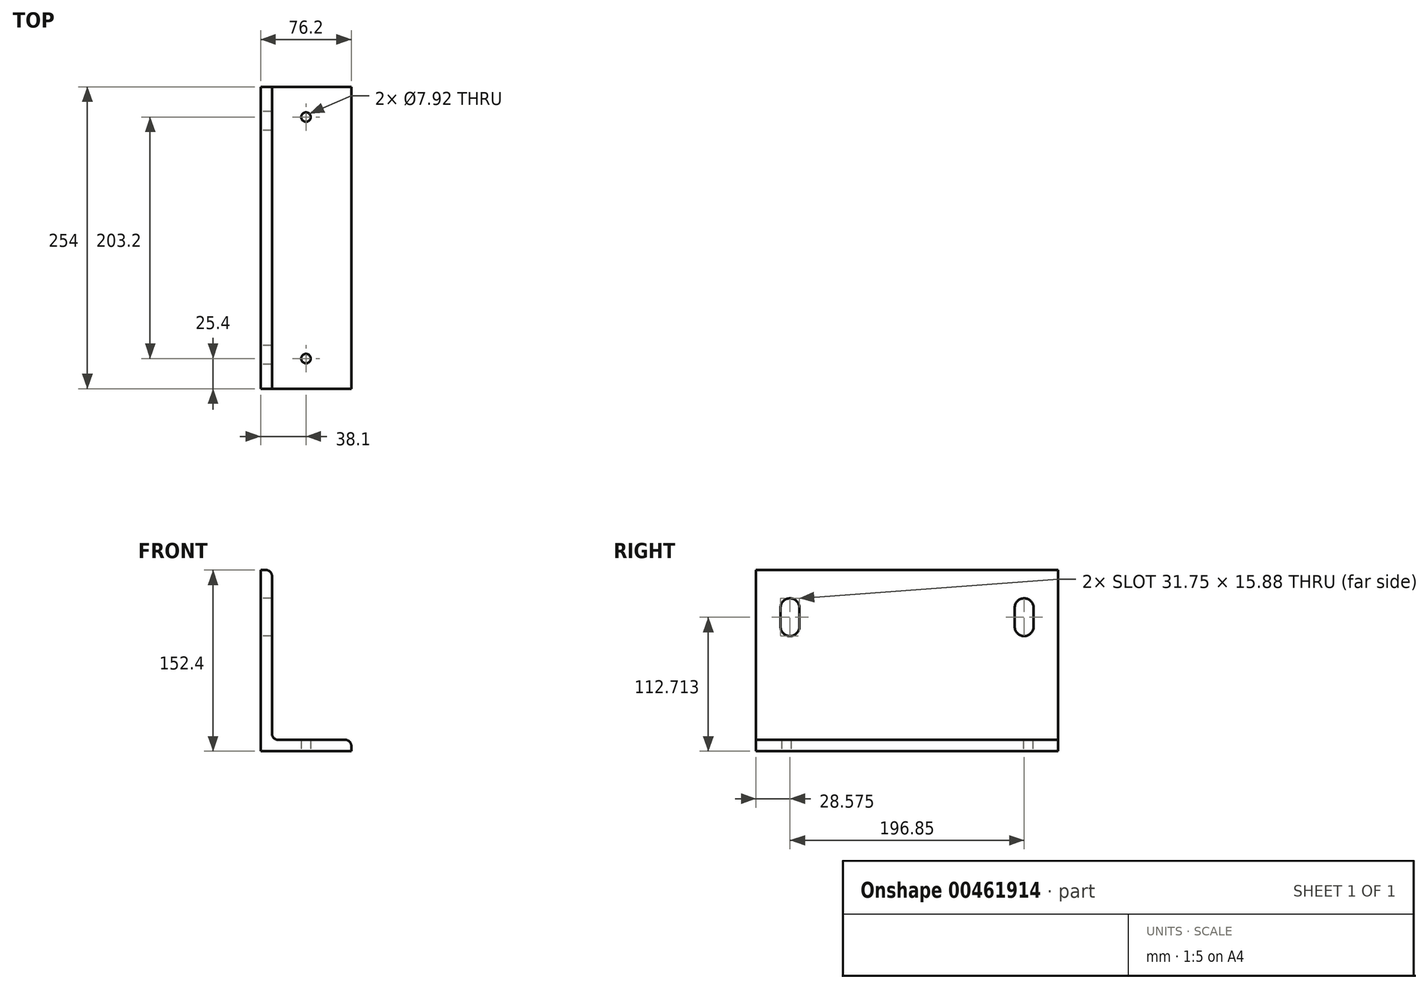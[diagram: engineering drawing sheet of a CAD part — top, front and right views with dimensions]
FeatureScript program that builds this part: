
annotation { "Feature Type Name" : "Feature", "Feature Type Description" : "" }
export const myFeature = defineFeature(function(context is Context, id is Id, definition is map)
    precondition{}
    {
        {
            var Q0;
            Q0=qCreatedBy(makeId("Front.planeOp"),FACE);
            var sketch = newSketch(context, id + "F0", { "sketchPlane" : qUnion([Q0])});
            skLineSegment(sketch, "E0", {"start": v(0, 0) * mm, "end": v(0, 152.4) * mm});
            skLineSegment(sketch, "E1", {"start": v(0, 152.4) * mm, "end": v(9.53, 152.4) * mm});
            skLineSegment(sketch, "E2", {"start": v(9.53, 152.4) * mm, "end": v(9.53, 9.53) * mm});
            skLineSegment(sketch, "E3", {"start": v(9.53, 9.53) * mm, "end": v(76.2, 9.53) * mm});
            skLineSegment(sketch, "E4", {"start": v(76.2, 9.53) * mm, "end": v(76.2, 0) * mm});
            skLineSegment(sketch, "E5", {"start": v(76.2, 0) * mm, "end": v(0, 0) * mm});
            skSolve(sketch);
        }
        {
            var Q0;
            Q0 = qSketchRegion(id + "F0", true);
            extrude(context, id + "F1", {"entities" : qUnion([Q0]), "endBound" : BoundingType.SYMMETRIC, "depth" : 254 * mm});
        }
        {
            var Q0;
            Q0=makeQuery(id+"F1.opExtrude","SWEPT_EDGE",EDGE,{"disambiguationData":[OSD([sQuery(id+"F0.wireOp",EDGE,"E1"),sQuery(id+"F0.wireOp",EDGE,"E2")])]});
            var Q1;
            Q1=makeQuery(id+"F1.opExtrude","SWEPT_EDGE",EDGE,{"disambiguationData":[OSD([sQuery(id+"F0.wireOp",EDGE,"E2"),sQuery(id+"F0.wireOp",EDGE,"E3")])]});
            var Q2;
            Q2=makeQuery(id+"F1.opExtrude","SWEPT_EDGE",EDGE,{"disambiguationData":[OSD([sQuery(id+"F0.wireOp",EDGE,"E3"),sQuery(id+"F0.wireOp",EDGE,"E4")])]});
            fillet(context, id + "F2", {"entities" : qUnion([Q0, Q1, Q2]), "radius" : 5.08 * mm, "tangentPropagation" : true, "allowEdgeOverflow" : false});
        }
        {
            var Q0;
            Q0=makeQuery(id+"F1.opExtrude","SWEPT_FACE",FACE,{"disambiguationData":[OSD([sQuery(id+"F0.wireOp",EDGE,"E0")])]});
            var sketch = newSketch(context, id + "F3", { "sketchPlane" : qUnion([Q0])});
            skArc(sketch, "E6", {"start": v(-90.49, 120.65) * mm, "mid": v(-98.42, 128.59) * mm, "end": v(-106.36, 120.65) * mm});
            skArc(sketch, "E7", {"start": v(-106.36, 104.78) * mm, "mid": v(-98.43, 96.84) * mm, "end": v(-90.49, 104.78) * mm});
            skLineSegment(sketch, "E8", {"start": v(-90.49, 104.78) * mm, "end": v(-90.49, 120.65) * mm});
            skLineSegment(sketch, "E9", {"start": v(-106.36, 104.78) * mm, "end": v(-106.36, 120.65) * mm});
            skArc(sketch, "E10.MirrorCS", {"start": v(90.49, 120.65) * mm, "mid": v(98.42, 128.59) * mm, "end": v(106.36, 120.65) * mm});
            skArc(sketch, "E11.MirrorCS", {"start": v(106.36, 104.78) * mm, "mid": v(98.43, 96.84) * mm, "end": v(90.49, 104.78) * mm});
            skLineSegment(sketch, "E12.MirrorCS", {"start": v(90.49, 104.78) * mm, "end": v(90.49, 120.65) * mm});
            skLineSegment(sketch, "E13.MirrorCS", {"start": v(106.36, 104.78) * mm, "end": v(106.36, 120.65) * mm});
            skSolve(sketch);
        }
        {
            var Q0;
            Q0 = qSketchRegion(id + "F3", true);
            extrude(context, id + "F4", {"entities" : qUnion([Q0]), "operationType" : NewBodyOperationType.REMOVE, "oppositeDirection" : true, "depth" : 25.4 * mm});
        }
        {
            var Q0;
            Q0=makeQuery(id+"F1.opExtrude","SWEPT_FACE",FACE,{"disambiguationData":[OSD([sQuery(id+"F0.wireOp",EDGE,"E5")])]});
            var sketch = newSketch(context, id + "F5", { "sketchPlane" : qUnion([Q0])});
            skCircle(sketch, "E14", {"center": v(38.1, -101.6) * mm, "radius": 3.96 * mm});
            skCircle(sketch, "E15.MirrorC", {"center": v(38.1, 101.6) * mm, "radius": 3.96 * mm});
            skSolve(sketch);
        }
        {
            var Q0;
            Q0 = qSketchRegion(id + "F5", true);
            extrude(context, id + "F6", {"entities" : qUnion([Q0]), "operationType" : NewBodyOperationType.REMOVE, "oppositeDirection" : true, "depth" : 25.4 * mm});
        }
    });
